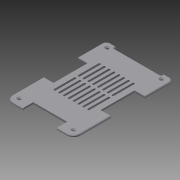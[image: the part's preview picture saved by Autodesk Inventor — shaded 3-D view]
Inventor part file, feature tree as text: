
AUTODESK INVENTOR PART (.ipt)
format: ipt  version: 2015 (Build 190159000, 159)  size: 367,616 bytes
history: native  units: mm
features: extrude x7, sketch x7, fillet x6, hole x4, chamfer x2, pattern_linear x1
ambient origin geometry x8: Origin, YZ Plane, XZ Plane, XY Plane, X Axis, Y Axis, Z Axis, Center Point
bodies: Volumenkörper1 (feature_tree)
feature tree (27):
  extrude  "Extrusion1"  Depth=10.0mm
  fillet  "Rundung2"  Radius=2.5mm
  fillet  "Rundung3"  Radius=10.0mm
  extrude  "Extrusion2"  Depth=3.0mm
  extrude  "Extrusion11"  Depth=3.0mm
  fillet  "Rundung9"  Radius=3.0mm
  extrude  "Extrusion13"  Depth=140.0mm
  pattern_linear  "Rechteckige Anordnung1"  Count1=9  [1 undecoded]
  chamfer  "Fase1"  Distance=90.0mm
  extrude  "Extrusion14"  Depth=10.0mm
  fillet  "Rundung10"  Radius=6.0mm
  extrude  "Extrusion15"  Depth=10.0mm
  fillet  "Rundung11"  Radius=4.0mm
  fillet  "Rundung12"  Radius=15.1mm
  extrude  "Extrusion16"  Depth=10.0mm
  chamfer  "Fase2"  Distance=15.1mm
  hole  "Bohrung6"  [1 undecoded]
  hole  "Bohrung7"  [1 undecoded]
  hole  "Bohrung8"  [1 undecoded]
  hole  "Bohrung9"  [1 undecoded]
  sketch  "Skizze1"  dims[d0=145.0mm d1=100.0mm d2=2.5mm d3=0.0mm d10=10.0mm]
  sketch  "Skizze3"  dims[d11=5.0mm d12=3.0mm]
  sketch  "Skizze10"  dims[d14=3.0mm d19=3.0mm d22=3.0mm]
  sketch  "Skizze12"  dims[d23=140.0mm d25=140.0mm]
  sketch  "Skizze13"  dims[d30=10.0mm]
  sketch  "Skizze14"  dims[d33=10.0mm d34=90.0mm]
  sketch  "Skizze15"  dims[d37=10.0mm d42=90.0mm d44=10.0mm d45=6.0mm d46=0.0mm d154=4.0mm d155=4.0mm d162=15.1mm d163=50.1mm d164=15.1mm d165=50.1mm d167=4.95mm d168=15.1mm d171=50.1mm d187=10.0mm d188=0.0mm d190=1.0mm d191=10.0mm d192=10.0mm d239=30.0mm d240=30.0mm d241=6.0mm d242=3.0mm d243=3.0mm d244=47.0mm d245=25.0mm d246=25.0mm d247=10.0mm d248=0.0mm d249=80.0mm d251=7.15mm d252=0.5mm d253=2.0mm d254=45.0deg d291=4.0mm d292=4.0mm d293=4.0mm d294=4.0mm d297=4.0mm d298=4.0mm d299=41.0mm d300=41.0mm d301=24.0mm d302=24.0mm d303=4.0mm d304=4.0mm d305=24.0mm d306=24.0mm d307=11.0mm d308=11.0mm d309=7.0mm d310=0.0mm d311=2.0mm d312=15.0mm d313=15.0mm d314=3.0mm d315=0.0mm d316=2.0mm d317=2.0mm d318=0.05mm d319=0.05mm d320=0.1mm d321=0.05mm d322=0.05mm d323=0.1mm d324=0.05mm d325=0.05mm d326=0.1mm d327=10.0mm d328=0.0mm d329=1.0mm d330=2.0mm d331=45.0deg d332=10.0mm d333=10.0mm d334=3.4mm d335=6.0mm d336=6.65mm d337=2.0mm d338=90.0deg d339=8.0mm d340=20.594885mm d341=10.0mm d342=10.0mm d343=3.4mm d344=6.0mm d345=6.65mm d346=2.0mm d347=90.0deg d348=8.0mm d349=20.594885mm d350=8.0mm d351=10.0mm d352=3.4mm d353=6.0mm d354=6.65mm d355=2.0mm d356=90.0deg d357=8.0mm d358=20.594885mm d359=8.0mm d360=10.0mm d361=3.4mm d362=6.0mm d363=6.65mm d364=2.0mm d365=90.0deg d366=8.0mm d367=20.594885mm]
note: 5 required parameter values undecoded (feature->parameter linkage not recoverable at this tier; creation-order binding heuristic only, values carry confidence <= 0.55)
